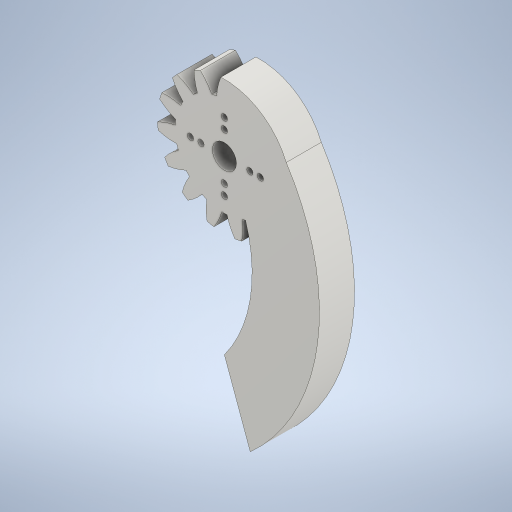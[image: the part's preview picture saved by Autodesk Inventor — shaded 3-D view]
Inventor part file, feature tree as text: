
AUTODESK INVENTOR PART (.ipt)
format: ipt  version: 2024 (Build 280153000, 153)  size: 686,080 bytes
history: native  units: mm (DEFAULTED — no unit token found)
features: other x7, extrude x3, plane x3, sketch x3, reference x1, projected_geometry x1
ambient origin geometry x8: Origin, YZ Plane, XZ Plane, XY Plane, X Axis, Y Axis, Z Axis, Center Point
bodies: Solid1 (feature_tree)
feature tree (18):
  extrude  "Extrusion1"  Depth=6.666667mm TaperAngle=0.0deg
  plane  "Work Plane2"
  plane  "Work Plane8"
  plane  "Work Plane9"
  other  "Spur Gear"
  extrude  "Extrusion2"  Depth=10.0mm TaperAngle=0.0deg
  extrude  "Extrusion3"  TaperAngle=0.0deg  [1 undecoded]
  sketch  "Sketch1"  dims[d0=25.49mm d1=6.666667mm d2=0.0mm]
  other  "Srf1"
  sketch  "Sketch3"  dims[d3=22.5mm d4=10.0mm d5=0.0mm]
  reference  "Reference1"
  sketch  "Sketch4"  dims[d16=23.4mm d17=0.0mm d34=2.094395mm d39=0.0mm d41=0.0mm d43=23.4mm d46=23.4mm d47=0.0mm d48=0.0mm d49=10.0mm d50=0.0mm d51=50.0mm d52=79.653867mm d53=54.037661mm d54=6.666667mm d55=0.0mm d61=3.490659mm d62=21.741525mm d63=27.373048mm d65=4.85mm d66=16.630991mm]
  projected_geometry  "Projected Loop1"
  other  "Pitch Diameter"
  other  "<userpath> windows\Documents\Inventor\Robotska_roka\roka_asemb.iam"
  other  "roka_asemb.iam"
  other  "SG90 - Micro Servo 9g - Tower Pro:2"
  other  "SG90 - Micro Servo 9g - Tower Pro.4"
note: 1 required parameter value undecoded (feature->parameter linkage not recoverable at this tier; creation-order binding heuristic only, values carry confidence <= 0.55)
